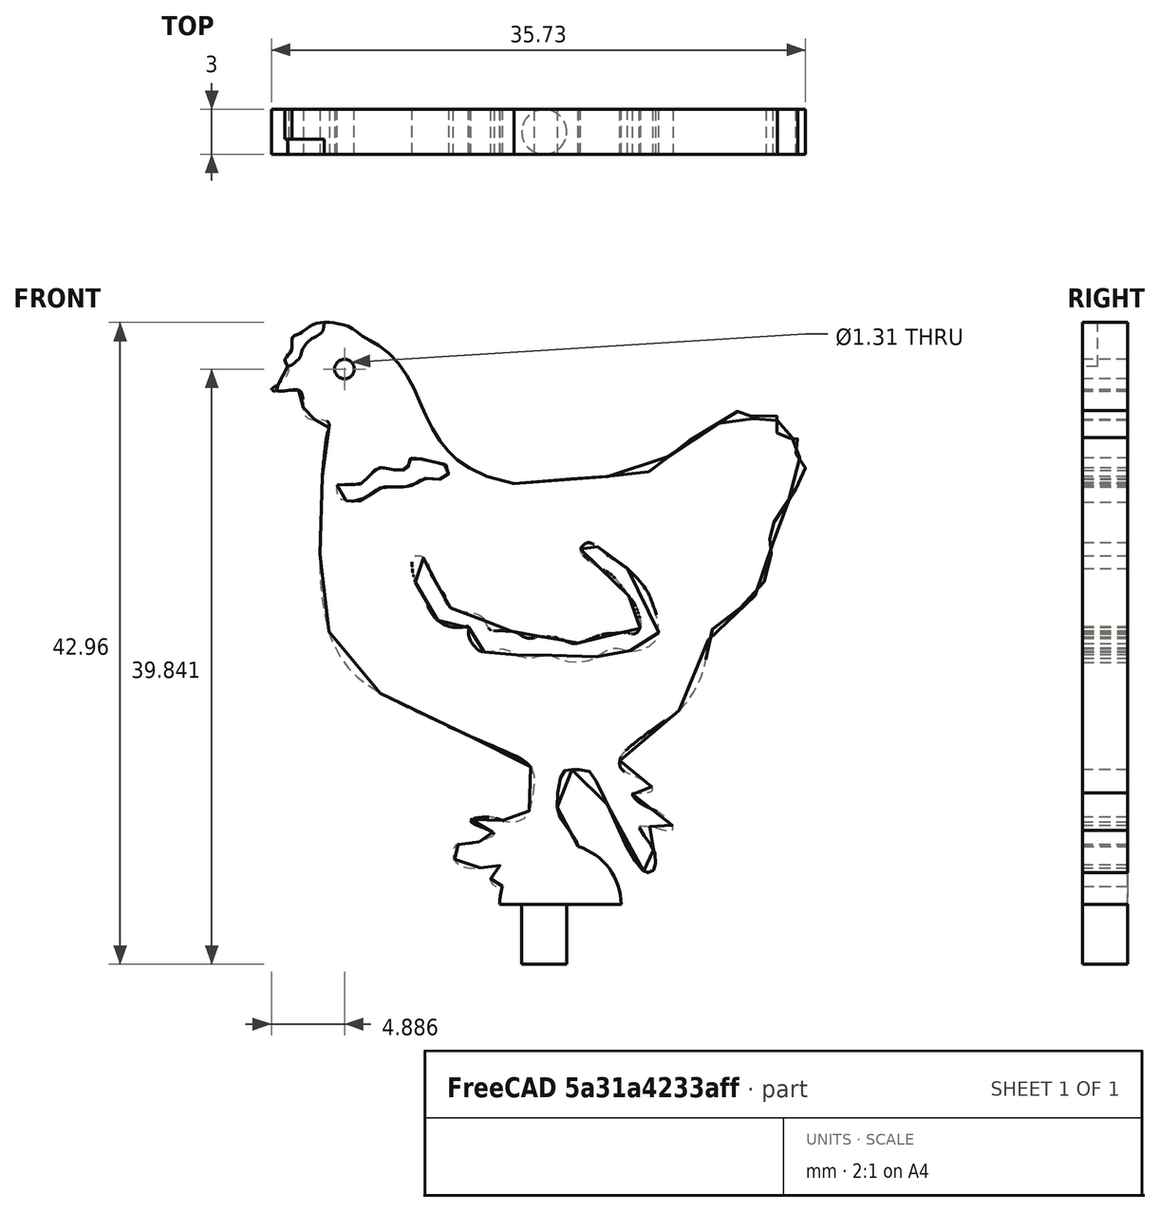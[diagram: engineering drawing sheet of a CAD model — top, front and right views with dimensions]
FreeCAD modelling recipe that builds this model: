
FCSTD DOCUMENT  (FreeCAD 0.19R)
Label: Poule
License: All rights reserved
LicenseURL: http://en.wikipedia.org/wiki/All_rights_reserved
objects: Sketcher::SketchObject×5, PartDesign::Pad×3, PartDesign::Pocket×2, Mesh::Feature×1, Part::Feature×1, PartDesign::Body×1
note: 17 computed .brp shape members not serialized (recipe doc carries the construction recipe); baked Part::Feature solids carry a one-line shape summary decoded from their .brp

FEATURE [Mesh::Feature] Hen
FEATURE [Part::Feature] Hen001
  Placement = pos=(-1,0,2) rot=(0,-1,0;1.5708rad)
  shape: bbox 35.51 x 1 x 38.09 mm, 4944 faces, 0 solids (baked)
FEATURE [Sketcher::SketchObject] Sketch
  FullyConstrained = false
  MapMode = 5
  Placement = pos=(0,0,0) rot=(1,0,0;1.5708rad)
  Support = -> [XZ_Plane]
  sketch-geometry (359):
    g0-g179: Circle x180 (B-spline internal-alignment scaffolding for g180; pole/knot coordinates omitted)
    g180: BSplineCurve PolesCount=180 KnotsCount=178 Degree=3 IsPeriodic=0
    g181-g358: GeomPoint x178 (B-spline internal-alignment scaffolding for g180; pole/knot coordinates omitted)
  constraints (169):
    c: Weight(g0) = 1
    c: Equal(g0, g1-g9) x9
    c: PointOnObject(g9,g8)
    c: Equal(g0,g10)
    c: Equal(g0,g11)
    c: PointOnObject(g11,g10)
    c: Equal(g0,g12)
    c: Equal(g0,g13)
    c: Equal(g0,g14)
    c: PointOnObject(g14,g12)
    c: Equal(g0,g15)
    c: Equal(g0,g16)
    c: PointOnObject(g16,g14)
    c: Equal(g0,g17)
    c: Equal(g0,g18)
    c: Equal(g0,g19)
    c: PointOnObject(g19,g16)
    c: Equal(g0,g20)
    c: PointOnObject(g20,g17)
    c: Equal(g0,g21)
    c: PointOnObject(g21,g19)
    c: Equal(g0,g22)
    c: Equal(g0,g23)
    c: Equal(g0,g24)
    c: PointOnObject(g24,g21)
    c: Equal(g0, g25-g30) x6
    c: PointOnObject(g30,g28)
    c: Equal(g0,g31)
    c: PointOnObject(g31,g29)
    c: Equal(g0,g32)
    c: PointOnObject(g32,g30)
    c: Equal(g0,g33)
    c: Equal(g0,g34)
    c: PointOnObject(g34,g32)
    c: Equal(g0,g35)
    c: PointOnObject(g35,g33)
    c: Equal(g0, g36-g49) x14
    c: PointOnObject(g49,g48)
    c: Equal(g0, g50-g56) x7
    c: PointOnObject(g56,g55)
    c: Equal(g0,g57)
    c: Equal(g0,g58)
    c: Equal(g0,g59)
    c: PointOnObject(g59,g55)
    c: Equal(g0, g60-g65) x6
    c: PointOnObject(g65,g63)
    c: Equal(g0,g66)
    c: Equal(g0,g67)
    c: PointOnObject(g67,g64)
    c: Equal(g0,g68)
    c: PointOnObject(g68,g66)
    c: Equal(g0,g69)
    c: PointOnObject(g69,g68)
    c: Equal(g0,g70)
    c: Equal(g0,g71)
    c: Equal(g0,g72)
    c: PointOnObject(g72,g70)
    c: Equal(g0,g73)
    c: Equal(g0,g74)
    c: PointOnObject(g74,g72)
    c: Equal(g0,g75)
    c: PointOnObject(g75,g73)
    c: Equal(g0,g76)
    c: Equal(g0,g77)
    c: PointOnObject(g77,g74)
    c: Equal(g0,g78)
    c: PointOnObject(g78,g76)
    c: Equal(g0,g79)
    c: PointOnObject(g79,g78)
    c: Equal(g0, g80-g84) x5
    c: PointOnObject(g84,g82)
    c: Equal(g0,g85)
    c: PointOnObject(g85,g82)
    c: Equal(g0,g86)
    c: PointOnObject(g86,g85)
    c: Equal(g0,g87)
    c: PointOnObject(g87,g86)
    c: Equal(g0,g88)
    c: Equal(g0,g89)
    c: PointOnObject(g89,g88)
    c: Equal(g0, g90-g93) x4
    c: PointOnObject(g93,g91)
    c: Equal(g0, g94-g98) x5
    c: PointOnObject(g98,g97)
    c: Equal(g0,g99)
    c: Equal(g0,g100)
    c: Equal(g0,g101)
    c: PointOnObject(g101,g99)
    c: Equal(g0,g102)
    c: Equal(g0,g103)
    c: PointOnObject(g103,g100)
    c: Equal(g0, g104-g109) x6
    c: PointOnObject(g109,g106)
    c: Equal(g0,g110)
    c: Equal(g0,g111)
    c: PointOnObject(g111,g109)
    c: Equal(g0,g112)
    c: Equal(g0,g113)
    c: PointOnObject(g113,g109)
    c: Equal(g0,g114)
    c: PointOnObject(g114,g113)
    c: Equal(g0,g115)
    c: PointOnObject(g115,g114)
    c: Equal(g0,g116)
    c: PointOnObject(g116,g115)
    c: Equal(g0,g117)
    c: Equal(g0,g118)
    c: PointOnObject(g118,g115)
    c: Equal(g0,g119)
    c: PointOnObject(g119,g115)
    c: Equal(g0,g120)
    c: PointOnObject(g120,g118)
    c: Equal(g0,g121)
    c: PointOnObject(g121,g118)
    c: Equal(g0,g122)
    c: PointOnObject(g122,g118)
    c: Equal(g0, g123-g126) x4
    c: PointOnObject(g126,g124)
    c: Equal(g0, g127-g130) x4
    c: PointOnObject(g130,g129)
    c: Equal(g0, g131-g135) x5
    c: PointOnObject(g135,g134)
    c: Equal(g0, g136-g140) x5
    c: PointOnObject(g140,g139)
    c: Equal(g0,g141)
    c: Equal(g0,g142)
    c: PointOnObject(g142,g140)
    c: Equal(g0,g143)
    c: PointOnObject(g143,g141)
    c: Equal(g0,g144)
    c: PointOnObject(g144,g142)
    c: Equal(g0, g145-g149) x5
    c: PointOnObject(g149,g147)
    c: Equal(g0,g150)
    c: Equal(g0,g151)
    c: PointOnObject(g151,g149)
    c: Equal(g0, g152-g155) x4
    c: PointOnObject(g155,g151)
    c: Equal(g0,g156)
    c: PointOnObject(g156,g154)
    c: Equal(g0,g157)
    c: PointOnObject(g157,g155)
    c: Equal(g0,g158)
    c: Equal(g0,g159)
    c: Equal(g0,g160)
    c: PointOnObject(g160,g157)
    c: Equal(g0,g161)
    c: Equal(g0,g162)
    c: PointOnObject(g162,g160)
    c: Equal(g0,g163)
    c: PointOnObject(g163,g161)
    c: Equal(g0,g164)
    c: PointOnObject(g164,g162)
    c: Equal(g0,g165)
    c: Equal(g0,g166)
    c: Equal(g0,g167)
    c: PointOnObject(g167,g166)
    c: Equal(g0,g168)
    c: PointOnObject(g168,g167)
    c: Equal(g0,g169)
    c: PointOnObject(g169,g168)
    c: Equal(g0,g170)
    c: PointOnObject(g170,g169)
    c: Equal(g0, g171-g178) x8
    c: PointOnObject(g178,g177)
    c: Equal(g0,g179)
    c: InternalAlignment(g0-g179 -> g180) x180
    c: InternalAlignment(g181-g358 -> g180) x178
    c: Coincident(g180,g180)
FEATURE [PartDesign::Pad] Pad
  Direction = (1,1,1)
  Length = 3
  Length2 = 100
  Placement = pos=(0,0,0) rot=(1,0,0;1.5708rad)
  Profile = -> Sketch
  Type = 0
FEATURE [Sketcher::SketchObject] Sketch001
  FullyConstrained = false
  MapMode = 5
  Placement = pos=(0,-3,1.3e-15) rot=(1,0,0;1.5708rad)
  Support = -> [Pad]
  sketch-geometry (215):
    g0: Circle CenterX=-13.3636 CenterY=35.8411 CenterZ=0 NormalX=0 NormalY=0 NormalZ=1 AngleXU=0 Radius=0.654235
    g1-g75: Circle x75 (B-spline internal-alignment scaffolding for g76; pole/knot coordinates omitted)
    g76: BSplineCurve PolesCount=75 KnotsCount=73 Degree=3 IsPeriodic=0
    g77-g149: GeomPoint x73 (B-spline internal-alignment scaffolding for g76; pole/knot coordinates omitted)
    g150-g182: Circle x33 (B-spline internal-alignment scaffolding for g183; pole/knot coordinates omitted)
    g183: BSplineCurve PolesCount=33 KnotsCount=31 Degree=3 IsPeriodic=0
    g184-g214: GeomPoint x31 (B-spline internal-alignment scaffolding for g183; pole/knot coordinates omitted)
  constraints (135):
    c: Weight(g1) = 1
    c: Equal(g1, g2-g5) x4
    c: PointOnObject(g5,g4)
    c: Equal(g1,g6)
    c: Equal(g1,g7)
    c: PointOnObject(g7,g6)
    c: Equal(g1, g8-g12) x5
    c: PointOnObject(g12,g11)
    c: Equal(g1,g13)
    c: Equal(g1,g14)
    c: PointOnObject(g14,g13)
    c: Equal(g1,g15)
    c: Equal(g1,g16)
    c: Equal(g1,g17)
    c: PointOnObject(g17,g16)
    c: Equal(g1,g18)
    c: Equal(g1,g19)
    c: Equal(g1,g20)
    c: PointOnObject(g20,g19)
    c: Equal(g1,g21)
    c: Equal(g1,g22)
    c: PointOnObject(g22,g20)
    c: Equal(g1,g23)
    c: PointOnObject(g23,g22)
    c: Equal(g1,g24)
    c: Equal(g1,g25)
    c: Equal(g1,g26)
    c: PointOnObject(g26,g25)
    c: Equal(g1,g27)
    c: Equal(g1,g28)
    c: PointOnObject(g28,g27)
    c: Equal(g1,g29)
    c: Equal(g1,g30)
    c: PointOnObject(g30,g29)
    c: Equal(g1,g31)
    c: Equal(g1,g32)
    c: Equal(g1,g33)
    c: PointOnObject(g33,g31)
    c: Equal(g1,g34)
    c: Equal(g1,g35)
    c: Equal(g1,g36)
    c: PointOnObject(g36,g34)
    c: Equal(g1,g37)
    c: Equal(g1,g38)
    c: Equal(g1,g39)
    c: PointOnObject(g39,g37)
    c: Equal(g1,g40)
    c: Equal(g1,g41)
    c: PointOnObject(g41,g25)
    c: Equal(g1,g42)
    c: PointOnObject(g42,g24)
    c: Equal(g1,g43)
    c: Equal(g1,g44)
    c: Equal(g1,g45)
    c: PointOnObject(g45,g43)
    c: Equal(g1,g46)
    c: PointOnObject(g46,g45)
    c: Equal(g1,g47)
    c: Equal(g1,g48)
    c: PointOnObject(g48,g46)
    c: Equal(g1,g49)
    c: Equal(g1,g50)
    c: PointOnObject(g50,g49)
    c: Equal(g1,g51)
    c: Equal(g1,g52)
    c: Equal(g1,g53)
    c: PointOnObject(g53,g52)
    c: Equal(g1,g54)
    c: PointOnObject(g54,g10)
    c: Equal(g1,g55)
    c: PointOnObject(g55,g10)
    c: Equal(g1,g56)
    c: Equal(g1,g57)
    c: PointOnObject(g57,g55)
    c: Equal(g1,g58)
    c: Equal(g1,g59)
    c: PointOnObject(g59,g57)
    c: Equal(g1,g60)
    c: Equal(g1,g61)
    c: Equal(g1,g62)
    c: PointOnObject(g62,g61)
    c: Equal(g1,g63)
    c: PointOnObject(g63,g62)
    c: Equal(g1, g64-g69) x6
    c: PointOnObject(g69,g66)
    c: Equal(g1,g70)
    c: PointOnObject(g70,g67)
    c: Equal(g1,g71)
    c: PointOnObject(g71,g69)
    c: Equal(g1,g72)
    c: PointOnObject(g72,g65)
    c: Equal(g1,g73)
    c: PointOnObject(g73,g64)
    c: Equal(g1,g74)
    c: Equal(g1,g75)
    c: PointOnObject(g76,g63)
    c: InternalAlignment(g1-g75 -> g76) x75
    c: InternalAlignment(g77-g149 -> g76) x73
    c: Coincident(g76,g76)
    c: Weight(g150) = 1
    c: Equal(g150,g151)
    c: Equal(g150,g152)
    c: PointOnObject(g152,g150)
    c: Equal(g150, g153-g157) x5
    c: PointOnObject(g157,g155)
    c: Equal(g150, g158-g161) x4
    c: PointOnObject(g161,g159)
    c: Equal(g150,g162)
    c: PointOnObject(g162,g160)
    c: Equal(g150,g163)
    c: Equal(g150,g164)
    c: Equal(g150,g165)
    c: PointOnObject(g165,g163)
    c: Equal(g150,g166)
    c: PointOnObject(g166,g164)
    c: Equal(g150, g167-g171) x5
    c: PointOnObject(g171,g161)
    c: Equal(g150,g172)
    c: PointOnObject(g172,g169)
    c: Equal(g150,g173)
    c: PointOnObject(g173,g170)
    c: Equal(g150, g174-g177) x4
    c: PointOnObject(g177,g156)
    c: Equal(g150,g178)
    c: PointOnObject(g178,g155)
    c: Equal(g150,g179)
    c: PointOnObject(g179,g155)
    c: Equal(g150,g180)
    c: PointOnObject(g180,g150)
    c: Equal(g150,g181)
    c: Equal(g150,g182)
    c: PointOnObject(g183,g151)
    c: InternalAlignment(g150-g182 -> g183) x33
    c: InternalAlignment(g184-g214 -> g183) x31
    c: Coincident(g183,g183)
FEATURE [PartDesign::Pocket] Pocket
  BaseFeature = -> Pad
  Length = 5
  Length2 = 100
  Placement = pos=(0,0,0) rot=(1,0,0;1.5708rad)
  Profile = -> Sketch001
  Type = 0
FEATURE [Sketcher::SketchObject] Sketch002
  FullyConstrained = false
  MapMode = 5
  Placement = pos=(0,-3,1.3e-15) rot=(1,0,0;1.5708rad)
  Support = -> [Pocket]
  sketch-geometry (2):
    g0: ArcOfCircle CenterX=1.08268 CenterY=0 CenterZ=0 NormalX=0 NormalY=0 NormalZ=1 AngleXU=0 Radius=4.06283 StartAngle=0 EndAngle=3.14159
    g1: LineSegment StartX=-2.98015 StartY=5e-16 StartZ=0 EndX=5.14551 EndY=0 EndZ=0
  constraints (5):
    c: PointOnObject(g0,g-1)
    c: PointOnObject(g0,g-1)
    c: PointOnObject(g0,g-1)
    c: Coincident(g1,g0)
    c: Coincident(g1,g0)
FEATURE [PartDesign::Pad] Pad001
  BaseFeature = -> Pocket
  Direction = (1,1,1)
  Length = 3
  Length2 = 100
  Placement = pos=(0,0,0) rot=(1,0,0;1.5708rad)
  Profile = -> Sketch002
  Reversed = true
  Type = 0
FEATURE [Sketcher::SketchObject] Sketch003
  FullyConstrained = true
  MapMode = 5
  Placement = pos=(0,0,3e-16) rot=(1,0,0;3.14159rad)
  Support = -> [Pad001]
  sketch-geometry (1):
    g0: Circle CenterX=0 CenterY=1.5 CenterZ=0 NormalX=0 NormalY=0 NormalZ=1 AngleXU=0 Radius=1.5
  constraints (3):
    c: PointOnObject(g0,g-2)
    c: Diameter(g0) = 3
    c: DistanceY(g-1,g0) = 1.5
FEATURE [PartDesign::Pad] Pad002
  BaseFeature = -> Pad001
  Direction = (1,1,1)
  Length = 4
  Length2 = 100
  Placement = pos=(0,0,0) rot=(1,0,0;1.5708rad)
  Profile = -> Sketch003
  Type = 0
FEATURE [Sketcher::SketchObject] Sketch004
  FullyConstrained = false
  MapMode = 5
  Placement = pos=(0,-3,1.3e-15) rot=(1,0,0;1.5708rad)
  Support = -> [Pad002]
  sketch-geometry (28):
    g0-g12: Circle x13 (B-spline internal-alignment scaffolding for g13; pole/knot coordinates omitted)
    g13: BSplineCurve PolesCount=13 KnotsCount=11 Degree=3 IsPeriodic=0
    g14-g24: GeomPoint x11 (B-spline internal-alignment scaffolding for g13; pole/knot coordinates omitted)
    g25: LineSegment StartX=-17.224 StartY=36.0223 StartZ=0 EndX=-17.687 EndY=37.1086 EndZ=0
    g26: LineSegment StartX=-17.687 StartY=37.1086 StartZ=0 EndX=-16.3745 EndY=38.999 EndZ=0
    g27: LineSegment StartX=-16.3745 StartY=38.999 StartZ=0 EndX=-14.7226 EndY=39.0108 EndZ=0
  constraints (10):
    c: Weight(g0) = 1
    c: Equal(g0, g1-g11) x11
    c: PointOnObject(g11,g7)
    c: Equal(g0,g12)
    c: InternalAlignment(g0-g12 -> g13) x13
    c: InternalAlignment(g14-g24 -> g13) x11
    c: Coincident(g25,g13)
    c: Coincident(g26,g25)
    c: Coincident(g27,g26)
    c: Coincident(g27,g13)
FEATURE [PartDesign::Pocket] Pocket001
  BaseFeature = -> Pad002
  Length = 1
  Length2 = 100
  Placement = pos=(0,0,0) rot=(1,0,0;1.5708rad)
  Profile = -> Sketch004
  Type = 0
FEATURE [PartDesign::Body] Body
  Group = -> [Sketch,Pad,Sketch001,Pocket,Sketch002,Pad001,Sketch003,Pad002,Sketch004,Pocket001]
  Origin = -> Origin
  Tip = -> Pocket001
